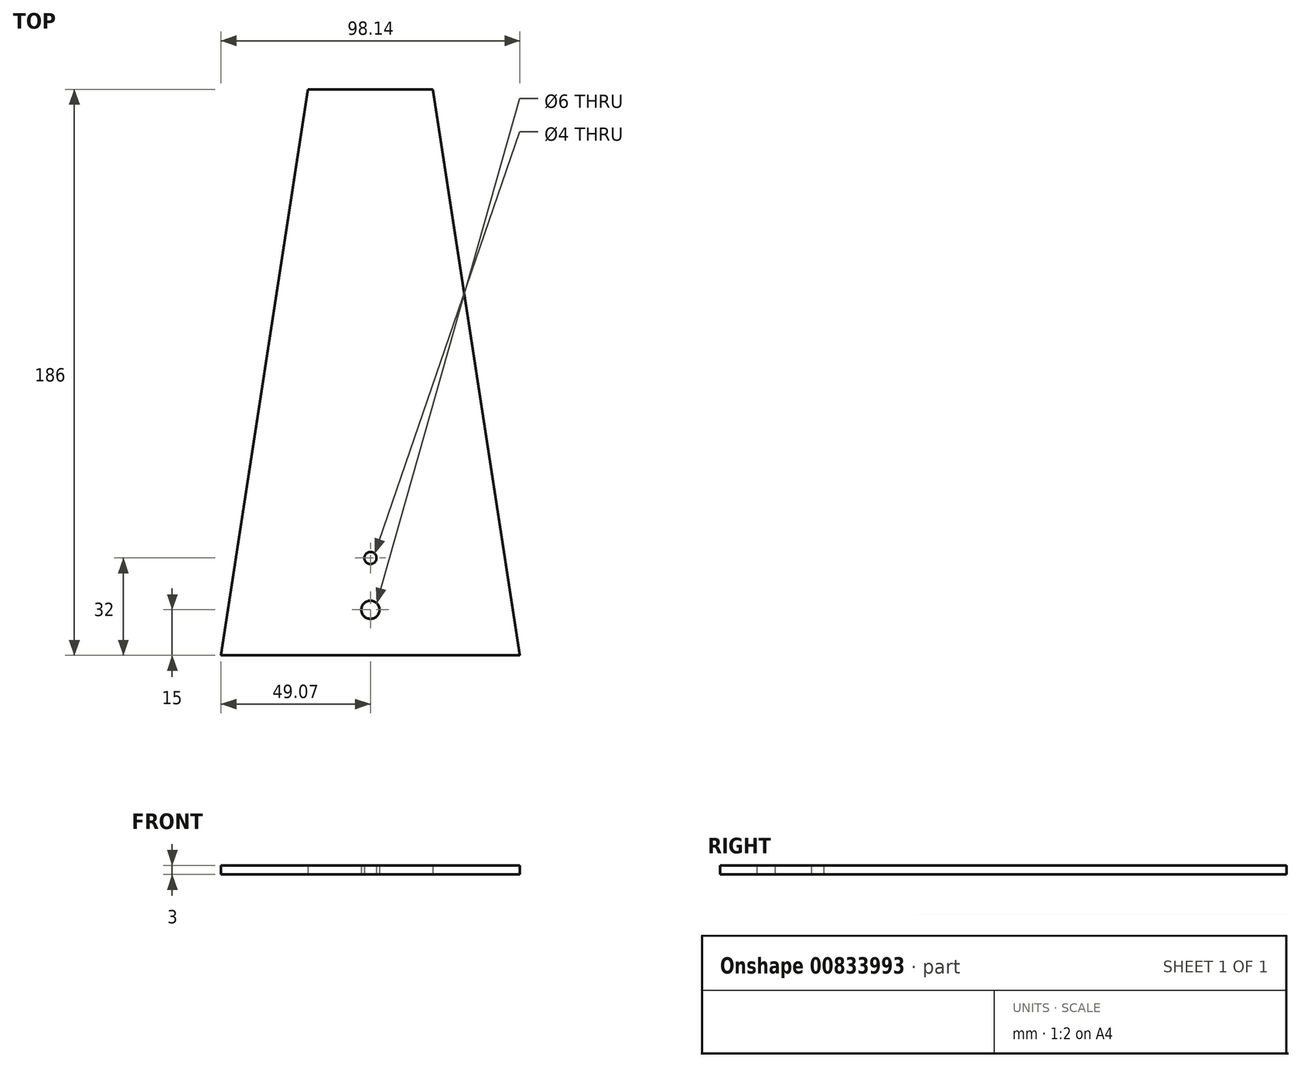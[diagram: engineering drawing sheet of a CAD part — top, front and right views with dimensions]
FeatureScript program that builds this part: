
annotation { "Feature Type Name" : "Feature", "Feature Type Description" : "" }
export const myFeature = defineFeature(function(context is Context, id is Id, definition is map)
    precondition{}
    {
        {
            var Q0;
            Q0=qCreatedBy(makeId("Top.planeOp"),FACE);
            var sketch = newSketch(context, id + "F0", { "sketchPlane" : qUnion([Q0])});
            skLineSegment(sketch, "E0", {"start": v(-46, 0) * mm, "end": v(-20.5, 166) * mm});
            skLineSegment(sketch, "E1", {"start": v(-20.5, 166) * mm, "end": v(20.5, 166) * mm});
            skLineSegment(sketch, "E2", {"start": v(20.5, 166) * mm, "end": v(49.07, -20) * mm});
            skLineSegment(sketch, "E3", {"start": v(46, 0) * mm, "end": v(-46, 0) * mm, "construction": true});
            skLineSegment(sketch, "E4", {"start": v(0, 166) * mm, "end": v(0, 0) * mm, "construction": true});
            skLineSegment(sketch, "E5", {"start": v(-46, 0) * mm, "end": v(-49.07, -20) * mm});
            skLineSegment(sketch, "E6", {"start": v(-49.07, -20) * mm, "end": v(49.07, -20) * mm});
            skCircle(sketch, "E7", {"center": v(0, -5) * mm, "radius": 3 * mm});
            skCircle(sketch, "E8", {"center": v(0, 12) * mm, "radius": 2 * mm});
            skSolve(sketch);
        }
        {
            var Q0;
            Q0=qSketchRegion(id+"F0",true);
            extrude(context, id + "F1", {"entities" : qUnion([Q0]), "depth" : 3 * mm, "offsetDistance" : 25 * mm});
        }
    });
